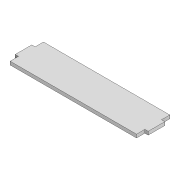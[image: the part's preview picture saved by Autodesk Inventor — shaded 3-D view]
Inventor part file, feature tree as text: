
AUTODESK INVENTOR PART (.ipt)
format: ipt  version: 2022 (Build 260153000, 153)  size: 86,528 bytes
history: native  units: mm
features: extrude x1, sketch x1
ambient origin geometry x8: Origin, YZ Plane, XZ Plane, XY Plane, X Axis, Y Axis, Z Axis, Center Point
bodies: Solid1 (feature_tree)
feature tree (2):
  extrude  "Extrusion1"  Depth=50.0mm
  sketch  "Sketch1"  dims[d0=190.0mm d1=50.0mm d2=5.0mm d3=25.0mm d4=12.5mm d5=5.0mm d6=0.0mm]
